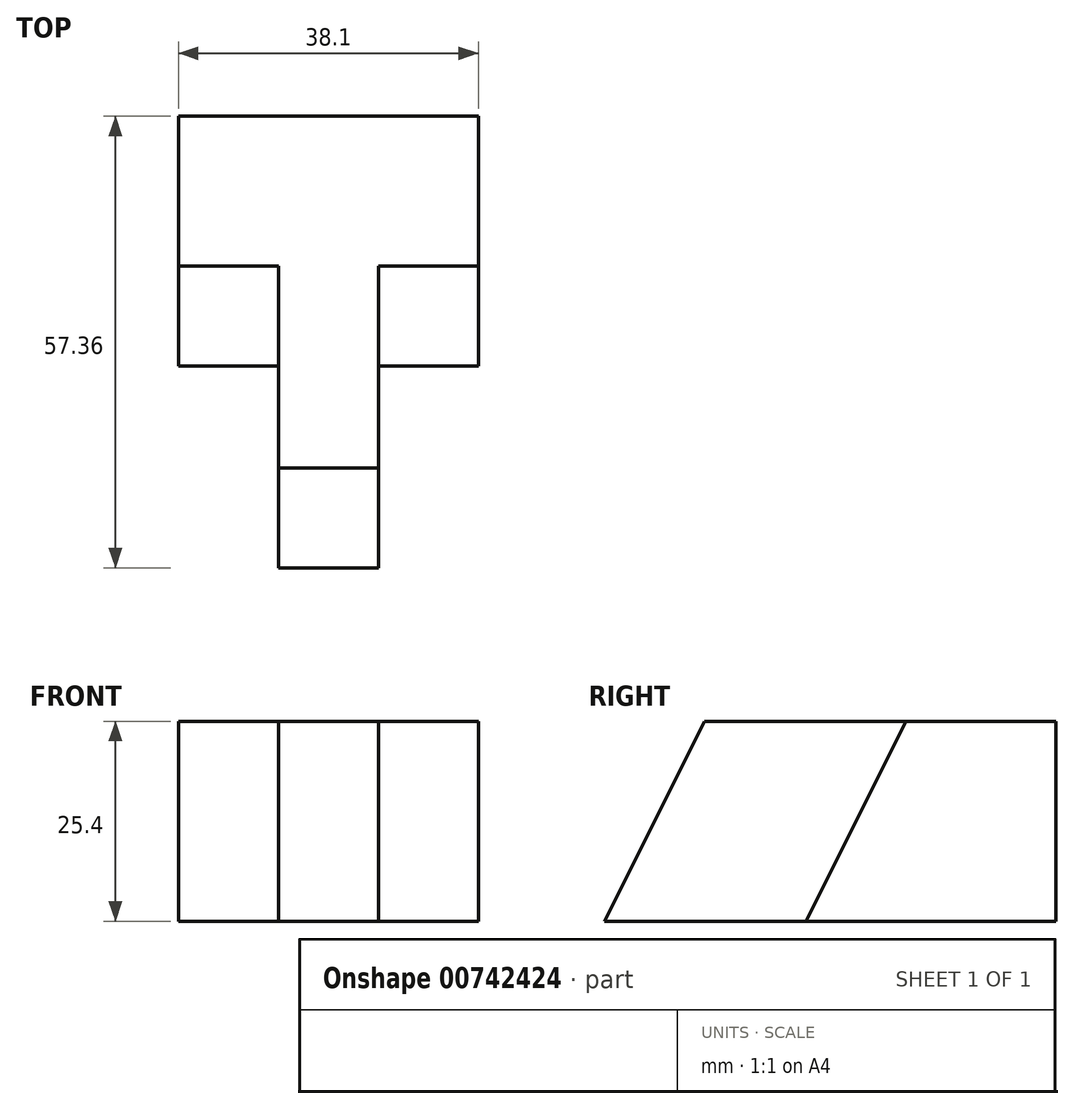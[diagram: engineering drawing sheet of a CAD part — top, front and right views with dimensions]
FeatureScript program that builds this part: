
annotation { "Feature Type Name" : "Feature", "Feature Type Description" : "" }
export const myFeature = defineFeature(function(context is Context, id is Id, definition is map)
    precondition{}
    {
        {
            var Q0;
            Q0=qCreatedBy(makeId("Top.planeOp"),FACE);
            var sketch = newSketch(context, id + "F0", { "sketchPlane" : qUnion([Q0])});
            skLineSegment(sketch, "E0", {"start": v(0, 57.36) * mm, "end": v(-27.46, 57.36) * mm});
            skLineSegment(sketch, "E1", {"start": v(-27.46, 57.36) * mm, "end": v(-27.46, 25.6) * mm});
            skLineSegment(sketch, "E2", {"start": v(-27.46, 25.6) * mm, "end": v(-14.76, 25.6) * mm});
            skLineSegment(sketch, "E3", {"start": v(-14.76, 25.6) * mm, "end": v(-14.76, 0) * mm});
            skLineSegment(sketch, "E4", {"start": v(-14.76, 0) * mm, "end": v(-2.06, 0) * mm});
            skLineSegment(sketch, "E5", {"start": v(-2.06, 0) * mm, "end": v(-2.06, 25.6) * mm});
            skLineSegment(sketch, "E6", {"start": v(-2.06, 25.6) * mm, "end": v(10.64, 25.6) * mm});
            skLineSegment(sketch, "E7", {"start": v(10.64, 25.6) * mm, "end": v(10.64, 57.36) * mm});
            skLineSegment(sketch, "E8", {"start": v(10.64, 57.36) * mm, "end": v(0, 57.36) * mm});
            skSolve(sketch);
        }
        {
            var Q0;
            Q0 = qSketchRegion(id + "F0", true);
            extrude(context, id + "F1", {"entities" : qUnion([Q0]), "depth" : 25.4 * mm, "offsetDistance" : 25.4 * mm});
        }
        {
            var Q0;
            Q0=makeQuery(id+"F1.opExtrude","SWEPT_FACE",FACE,{"disambiguationData":[OSD([sQuery(id+"F0.wireOp",EDGE,"E1")])]});
            var sketch = newSketch(context, id + "F2", { "sketchPlane" : qUnion([Q0])});
            skLineSegment(sketch, "E9", {"start": v(-38.3, 25.4) * mm, "end": v(-25.6, 0) * mm});
            skSolve(sketch);
        }
        {
            var Q0;
            {var subQ0=sQuery(id+"F2.wireOp",EDGE,"E9");Q0=makeQuery(id+"F2.imprint","IMPRINT",FACE,{"disambiguationData":[TD([[makeQuery(id+"F2.imprint","IMPRINT",EDGE,{"derivedFrom":subQ0}),1.0]])]});}
            extrude(context, id + "F3", {"entities" : qUnion([Q0]), "operationType" : NewBodyOperationType.REMOVE, "oppositeDirection" : true, "depth" : 12.7 * mm, "offsetDistance" : 25.4 * mm});
        }
        {
            var Q0;
            Q0=makeQuery(id+"F1.opExtrude","SWEPT_FACE",FACE,{"disambiguationData":[OSD([sQuery(id+"F0.wireOp",EDGE,"E7")])]});
            var sketch = newSketch(context, id + "F4", { "sketchPlane" : qUnion([Q0])});
            skLineSegment(sketch, "E10", {"start": v(25.6, 0) * mm, "end": v(38.3, 25.4) * mm});
            skSolve(sketch);
        }
        {
            var Q0;
            {var subQ0=sQuery(id+"F4.wireOp",EDGE,"E10");Q0=makeQuery(id+"F4.imprint","IMPRINT",FACE,{"disambiguationData":[TD([[makeQuery(id+"F4.imprint","IMPRINT",EDGE,{"derivedFrom":subQ0}),1.0]])]});}
            extrude(context, id + "F5", {"entities" : qUnion([Q0]), "operationType" : NewBodyOperationType.REMOVE, "oppositeDirection" : true, "depth" : 12.7 * mm, "offsetDistance" : 25.4 * mm});
        }
        {
            var Q0;
            Q0=makeQuery(id+"F3.boolean.opBoolean","MERGE",FACE,{"derivedFrom":[makeQuery(id+"F1.opExtrude","SWEPT_FACE",FACE,{"disambiguationData":[OSD([sQuery(id+"F0.wireOp",EDGE,"E3")])]}),makeQuery(id+"F3.opExtrude","CAP_FACE",FACE,{"disambiguationData":[OSD([sQuery(id+"F0.wireOp",EDGE,"E1"),sQuery(id+"F0.wireOp",EDGE,"E2"),sQuery(id+"F2.wireOp",EDGE,"E9")])],"isStart":false})]});
            var sketch = newSketch(context, id + "F6", { "sketchPlane" : qUnion([Q0])});
            skLineSegment(sketch, "E11", {"start": v(-12.7, 25.4) * mm, "end": v(0, 0) * mm});
            skSolve(sketch);
        }
        {
            var Q0;
            {var subQ0=sQuery(id+"F6.wireOp",EDGE,"E11");Q0=makeQuery(id+"F6.imprint","IMPRINT",FACE,{"disambiguationData":[TD([[makeQuery(id+"F6.imprint","IMPRINT",EDGE,{"derivedFrom":subQ0}),1.0]])]});}
            extrude(context, id + "F7", {"entities" : qUnion([Q0]), "operationType" : NewBodyOperationType.REMOVE, "oppositeDirection" : true, "depth" : 12.7 * mm, "offsetDistance" : 25.4 * mm});
        }
    });
